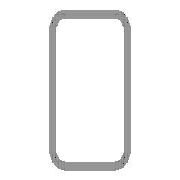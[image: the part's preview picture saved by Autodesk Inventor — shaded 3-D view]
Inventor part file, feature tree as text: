
AUTODESK INVENTOR PART (.ipt)
format: ipt  version: 2025 (Build 290162010, 162A)  size: 132,608 bytes
history: native  units: mm (DEFAULTED — no unit token found)
features: other x4, sketch x1, plane x1
ambient origin geometry x8: Origin, YZ Plane, XZ Plane, XY Plane, X Axis, Y Axis, Z Axis, Center Point
bodies: Solid1 (feature_tree), Body (feature_tree)
feature tree (6):
  parser-record x1  (decoder bookkeeping rows leaked as tree rows — omitted from the tree; the rows remain in map.json)
  other  "Driven Length"
  other  "Start Plane"
  other  "End Plane"
  sketch  "Sketch3"  dims[d3=1150.0mm d4=0.0mm d7=6.0mm d9=40.0mm d11=80.0mm d12=3.0mm d13=-0.0mm d14=1150.0mm d15=20.0mm d16=40.0mm d17=90.0deg d18=1150.0mm]
  plane  "Work Plane3"
